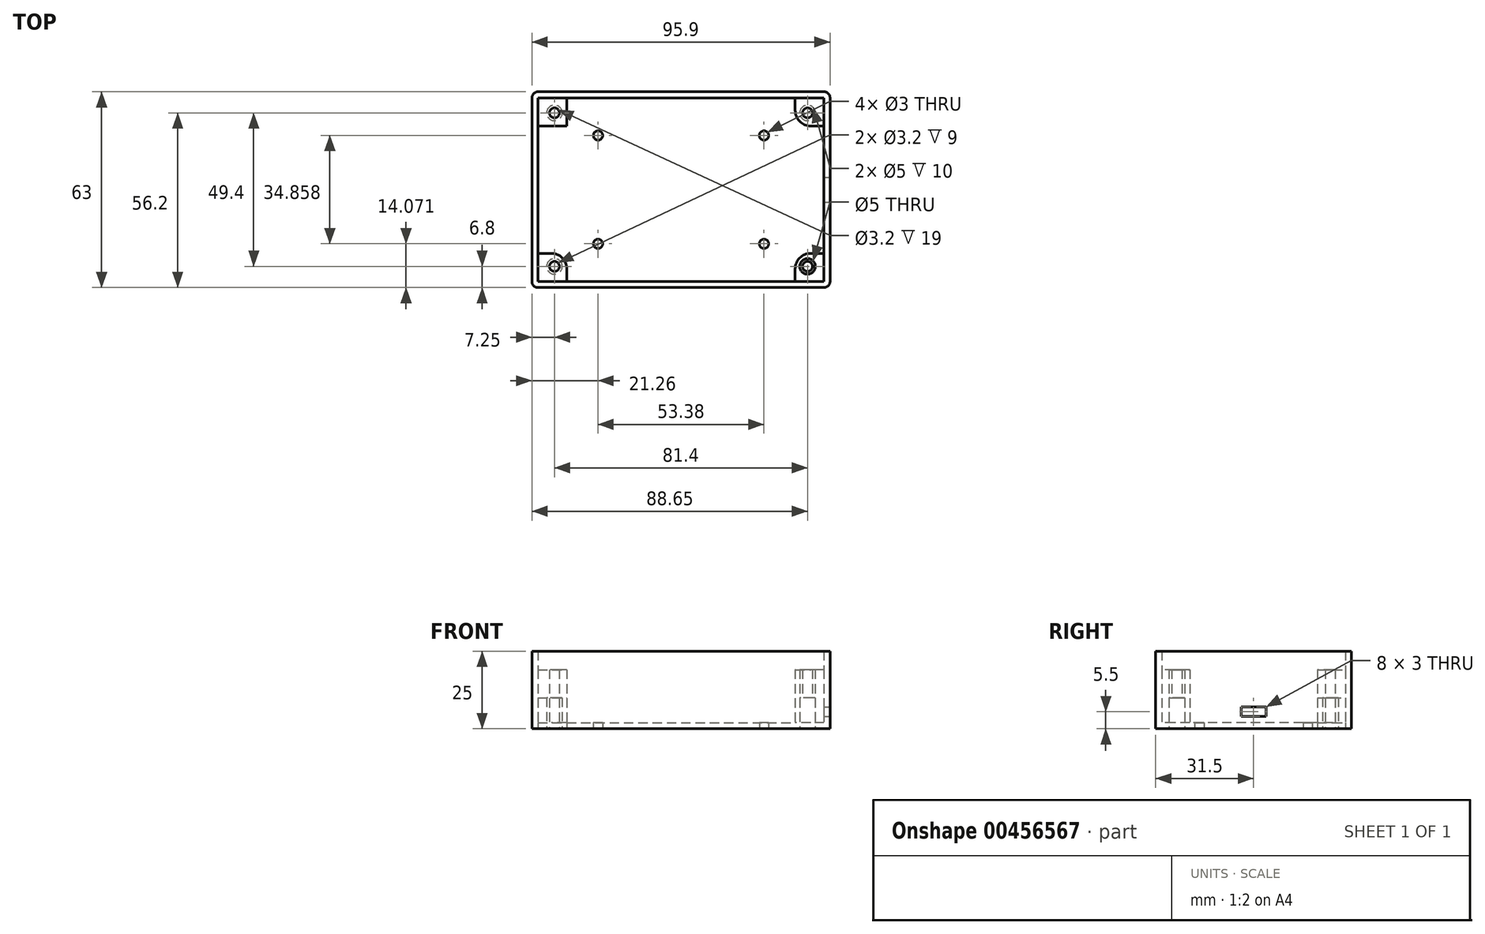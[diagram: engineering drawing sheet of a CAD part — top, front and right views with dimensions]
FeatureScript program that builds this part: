
annotation { "Feature Type Name" : "Feature", "Feature Type Description" : "" }
export const myFeature = defineFeature(function(context is Context, id is Id, definition is map)
    precondition{}
    {
        {
            var Q0;
            Q0=qCreatedBy(makeId("Top.planeOp"),FACE);
            var sketch = newSketch(context, id + "F0", { "sketchPlane" : qUnion([Q0])});
            skLineSegment(sketch, "E0", {"start": v(-47.95, 0) * mm, "end": v(-47.95, 31.5) * mm});
            skLineSegment(sketch, "E1", {"start": v(-47.95, 31.5) * mm, "end": v(0, 31.5) * mm});
            skLineSegment(sketch, "E2.MirrorCS", {"start": v(-47.95, -31.5) * mm, "end": v(0, -31.5) * mm});
            skLineSegment(sketch, "E3.MirrorCS", {"start": v(-47.95, 0) * mm, "end": v(-47.95, -31.5) * mm});
            skLineSegment(sketch, "E4.MirrorCS", {"start": v(47.95, 31.5) * mm, "end": v(0, 31.5) * mm});
            skLineSegment(sketch, "E5.MirrorCS", {"start": v(47.95, -31.5) * mm, "end": v(0, -31.5) * mm});
            skLineSegment(sketch, "E6.MirrorCS", {"start": v(47.95, 0) * mm, "end": v(47.95, -31.5) * mm});
            skLineSegment(sketch, "E7.MirrorCS", {"start": v(47.95, 0) * mm, "end": v(47.95, 31.5) * mm});
            skLineSegment(sketch, "E8", {"start": v(-46, 0) * mm, "end": v(-46, 29.5) * mm});
            skLineSegment(sketch, "E9", {"start": v(-46, 29.5) * mm, "end": v(0, 29.5) * mm});
            skLineSegment(sketch, "E10.MirrorCS", {"start": v(46, 29.5) * mm, "end": v(0, 29.5) * mm});
            skLineSegment(sketch, "E11.MirrorCS", {"start": v(46, 0) * mm, "end": v(46, 29.5) * mm});
            skLineSegment(sketch, "E12.MirrorCS", {"start": v(-46, 0) * mm, "end": v(-46, -29.5) * mm});
            skLineSegment(sketch, "E13.MirrorCS", {"start": v(-46, -29.5) * mm, "end": v(0, -29.5) * mm});
            skLineSegment(sketch, "E14.MirrorCS", {"start": v(46, -29.5) * mm, "end": v(0, -29.5) * mm});
            skLineSegment(sketch, "E15.MirrorCS", {"start": v(46, 0) * mm, "end": v(46, -29.5) * mm});
            skCircle(sketch, "E16", {"center": v(26.7, -17.43) * mm, "radius": 1.5 * mm});
            skCircle(sketch, "E17.MirrorC", {"center": v(-26.7, -17.43) * mm, "radius": 1.5 * mm});
            skCircle(sketch, "E18.MirrorC", {"center": v(-26.7, 17.43) * mm, "radius": 1.5 * mm});
            skCircle(sketch, "E19.MirrorC", {"center": v(26.7, 17.43) * mm, "radius": 1.5 * mm});
            skCircle(sketch, "E20", {"center": v(-40.7, -24.7) * mm, "radius": 1.6 * mm});
            skCircle(sketch, "E21", {"center": v(-40.7, -24.7) * mm, "radius": 2.5 * mm});
            skLineSegment(sketch, "E22", {"start": v(-46, -20.5) * mm, "end": v(-36.73, -20.5) * mm});
            skLineSegment(sketch, "E23", {"start": v(-36.73, -20.5) * mm, "end": v(-36.73, -29.5) * mm});
            skLineSegment(sketch, "E24.MirrorCS", {"start": v(36.73, -20.5) * mm, "end": v(36.73, -29.5) * mm});
            skLineSegment(sketch, "E25.MirrorCS", {"start": v(46, -20.5) * mm, "end": v(36.73, -20.5) * mm});
            skCircle(sketch, "E26.MirrorC", {"center": v(40.7, -24.7) * mm, "radius": 1.6 * mm});
            skCircle(sketch, "E27.MirrorC", {"center": v(40.7, -24.7) * mm, "radius": 2.5 * mm});
            skCircle(sketch, "E28.MirrorC", {"center": v(-40.7, 24.7) * mm, "radius": 2.5 * mm});
            skCircle(sketch, "E29.MirrorC", {"center": v(-40.7, 24.7) * mm, "radius": 1.6 * mm});
            skLineSegment(sketch, "E30.MirrorCS", {"start": v(-46, 20.5) * mm, "end": v(-36.73, 20.5) * mm});
            skLineSegment(sketch, "E31.MirrorCS", {"start": v(-36.73, 20.5) * mm, "end": v(-36.73, 29.5) * mm});
            skLineSegment(sketch, "E32.MirrorCS", {"start": v(46, 20.5) * mm, "end": v(36.73, 20.5) * mm});
            skLineSegment(sketch, "E33.MirrorCS", {"start": v(36.73, 20.5) * mm, "end": v(36.73, 29.5) * mm});
            skCircle(sketch, "E34.MirrorC", {"center": v(40.7, 24.7) * mm, "radius": 2.5 * mm});
            skCircle(sketch, "E35.MirrorC", {"center": v(40.7, 24.7) * mm, "radius": 1.6 * mm});
            skSolve(sketch);
        }
        {
            var Q0;
            Q0=makeQuery(id+"F0.imprint","IMPRINT",FACE,{"disambiguationData":[TD([[makeQuery(id+"F0.imprint","IMPRINT",EDGE,{"derivedFrom":sQuery(id+"F0.wireOp",EDGE,"E0")}),-1.0]])]});
            extrude(context, id + "F1", {"entities" : qUnion([Q0]), "depth" : 25 * mm});
        }
        {
            var Q0;
            Q0=makeQuery(id+"F1.opExtrude","SWEPT_EDGE",EDGE,{"disambiguationData":[OSD([sQuery(id+"F0.wireOp",EDGE,"E2.MirrorCS"),sQuery(id+"F0.wireOp",EDGE,"E3.MirrorCS")])]});
            fillet(context, id + "F2", {"entities" : qUnion([Q0]), "radius" : 2 * mm, "tangentPropagation" : true, "allowEdgeOverflow" : false});
        }
        {
            var Q0;
            Q0=makeQuery(id+"F1.opExtrude","SWEPT_EDGE",EDGE,{"disambiguationData":[OSD([sQuery(id+"F0.wireOp",EDGE,"E5.MirrorCS"),sQuery(id+"F0.wireOp",EDGE,"E6.MirrorCS")])]});
            var Q1;
            Q1=makeQuery(id+"F1.opExtrude","SWEPT_EDGE",EDGE,{"disambiguationData":[OSD([sQuery(id+"F0.wireOp",EDGE,"E4.MirrorCS"),sQuery(id+"F0.wireOp",EDGE,"E7.MirrorCS")])]});
            var Q2;
            Q2=makeQuery(id+"F1.opExtrude","SWEPT_EDGE",EDGE,{"disambiguationData":[OSD([sQuery(id+"F0.wireOp",EDGE,"E0"),sQuery(id+"F0.wireOp",EDGE,"E1")])]});
            fillet(context, id + "F3", {"entities" : qUnion([Q0, Q1, Q2]), "radius" : 2 * mm, "tangentPropagation" : true, "allowEdgeOverflow" : false});
        }
        {
            var Q0;
            Q0=makeQuery(id+"F0.imprint","IMPRINT",FACE,{"disambiguationData":[TD([[makeQuery(id+"F0.imprint","IMPRINT",EDGE,{"derivedFrom":sQuery(id+"F0.wireOp",EDGE,"E16")}),-1.0]])]});
            extrude(context, id + "F4", {"entities" : qUnion([Q0]), "operationType" : NewBodyOperationType.ADD, "depth" : 2 * mm});
        }
        {
            var Q0;
            Q0=makeQuery(id+"F0.imprint","IMPRINT",FACE,{"disambiguationData":[TD([[makeQuery(id+"F0.imprint","IMPRINT",EDGE,{"derivedFrom":sQuery(id+"F0.wireOp",EDGE,"E28.MirrorC")}),1.0]])]});
            var Q1;
            {var subQ1=sQuery(id+"F0.wireOp",EDGE,"E32.MirrorCS");Q1=makeQuery(id+"F0.imprint","IMPRINT",FACE,{"disambiguationData":[TD([[makeQuery(id+"F0.imprint","IMPRINT",EDGE,{"derivedFrom":subQ1}),-1.0]])]});}
            var Q2;
            {var subQ0=sQuery(id+"F0.wireOp",EDGE,"E24.MirrorCS");Q2=makeQuery(id+"F0.imprint","IMPRINT",FACE,{"disambiguationData":[TD([[makeQuery(id+"F0.imprint","IMPRINT",EDGE,{"derivedFrom":subQ0}),1.0]])]});}
            var Q3;
            Q3=makeQuery(id+"F0.imprint","IMPRINT",FACE,{"disambiguationData":[TD([[makeQuery(id+"F0.imprint","IMPRINT",EDGE,{"derivedFrom":sQuery(id+"F0.wireOp",EDGE,"E21")}),-1.0]])]});
            extrude(context, id + "F5", {"entities" : qUnion([Q0, Q1, Q2, Q3]), "operationType" : NewBodyOperationType.ADD, "depth" : 19 * mm});
        }
        {
            var Q0;
            Q0=makeQuery(id+"F5.opExtrude","SWEPT_EDGE",EDGE,{"disambiguationData":[OSD([sQuery(id+"F0.wireOp",EDGE,"E30.MirrorCS"),sQuery(id+"F0.wireOp",EDGE,"E31.MirrorCS")])]});
            var Q1;
            Q1=makeQuery(id+"F5.opExtrude","SWEPT_EDGE",EDGE,{"disambiguationData":[OSD([sQuery(id+"F0.wireOp",EDGE,"E32.MirrorCS"),sQuery(id+"F0.wireOp",EDGE,"E33.MirrorCS")])]});
            var Q2;
            Q2=makeQuery(id+"F5.opExtrude","SWEPT_EDGE",EDGE,{"disambiguationData":[OSD([sQuery(id+"F0.wireOp",EDGE,"E24.MirrorCS"),sQuery(id+"F0.wireOp",EDGE,"E25.MirrorCS")])]});
            var Q3;
            Q3=makeQuery(id+"F5.opExtrude","SWEPT_EDGE",EDGE,{"disambiguationData":[OSD([sQuery(id+"F0.wireOp",EDGE,"E22"),sQuery(id+"F0.wireOp",EDGE,"E23")])]});
            fillet(context, id + "F6", {"entities" : qUnion([Q0, Q1, Q2, Q3]), "radius" : 5 * mm, "tangentPropagation" : true, "allowEdgeOverflow" : false});
        }
        {
            var Q0;
            Q0=makeQuery(id+"F0.imprint","IMPRINT",FACE,{"disambiguationData":[TD([[makeQuery(id+"F0.imprint","IMPRINT",EDGE,{"derivedFrom":sQuery(id+"F0.wireOp",EDGE,"E28.MirrorC")}),-1.0]])]});
            var Q1;
            Q1=makeQuery(id+"F0.imprint","IMPRINT",FACE,{"disambiguationData":[TD([[makeQuery(id+"F0.imprint","IMPRINT",EDGE,{"derivedFrom":sQuery(id+"F0.wireOp",EDGE,"E34.MirrorC")}),1.0]])]});
            var Q2;
            Q2=makeQuery(id+"F0.imprint","IMPRINT",FACE,{"disambiguationData":[TD([[makeQuery(id+"F0.imprint","IMPRINT",EDGE,{"derivedFrom":sQuery(id+"F0.wireOp",EDGE,"E26.MirrorC")}),1.0]])]});
            var Q3;
            Q3=makeQuery(id+"F0.imprint","IMPRINT",FACE,{"disambiguationData":[TD([[makeQuery(id+"F0.imprint","IMPRINT",EDGE,{"derivedFrom":sQuery(id+"F0.wireOp",EDGE,"E20")}),-1.0]])]});
            extrude(context, id + "F7", {"entities" : qUnion([Q0, Q1, Q2, Q3]), "operationType" : NewBodyOperationType.ADD, "depth" : 19 * mm});
        }
        {
            var Q0;
            Q0=makeQuery(id+"F0.imprint","IMPRINT",FACE,{"disambiguationData":[TD([[makeQuery(id+"F0.imprint","IMPRINT",EDGE,{"derivedFrom":sQuery(id+"F0.wireOp",EDGE,"E28.MirrorC")}),-1.0]])]});
            var Q1;
            Q1=makeQuery(id+"F0.imprint","IMPRINT",FACE,{"disambiguationData":[TD([[makeQuery(id+"F0.imprint","IMPRINT",EDGE,{"derivedFrom":sQuery(id+"F0.wireOp",EDGE,"E20")}),-1.0]])]});
            var Q2;
            Q2=makeQuery(id+"F0.imprint","IMPRINT",FACE,{"disambiguationData":[TD([[makeQuery(id+"F0.imprint","IMPRINT",EDGE,{"derivedFrom":sQuery(id+"F0.wireOp",EDGE,"E26.MirrorC")}),1.0]])]});
            var Q3;
            Q3=makeQuery(id+"F0.imprint","IMPRINT",FACE,{"disambiguationData":[TD([[makeQuery(id+"F0.imprint","IMPRINT",EDGE,{"derivedFrom":sQuery(id+"F0.wireOp",EDGE,"E34.MirrorC")}),1.0]])]});
            extrude(context, id + "F8", {"entities" : qUnion([Q0, Q1, Q2, Q3]), "operationType" : NewBodyOperationType.REMOVE, "depth" : 10 * mm});
        }
        {
            var Q0;
            Q0=makeQuery(id+"F1.opExtrude","SWEPT_FACE",FACE,{"disambiguationData":[OSD([sQuery(id+"F0.wireOp",EDGE,"E6.MirrorCS"),sQuery(id+"F0.wireOp",EDGE,"E7.MirrorCS")])]});
            var sketch = newSketch(context, id + "F9", { "sketchPlane" : qUnion([Q0])});
            skLineSegment(sketch, "E36", {"start": v(0, 4) * mm, "end": v(-4, 4) * mm});
            skLineSegment(sketch, "E37", {"start": v(-4, 4) * mm, "end": v(-4, 7) * mm});
            skLineSegment(sketch, "E38", {"start": v(-4, 7) * mm, "end": v(0, 7) * mm});
            skLineSegment(sketch, "E39", {"start": v(0, 4) * mm, "end": v(0, 0) * mm});
            skLineSegment(sketch, "E40.MirrorCS", {"start": v(4, 7) * mm, "end": v(0, 7) * mm});
            skLineSegment(sketch, "E41.MirrorCS", {"start": v(4, 4) * mm, "end": v(4, 7) * mm});
            skLineSegment(sketch, "E42.MirrorCS", {"start": v(0, 4) * mm, "end": v(4, 4) * mm});
            skSolve(sketch);
        }
        {
            var Q0;
            Q0=makeQuery(id+"F9.imprint","IMPRINT",FACE,{"disambiguationData":[TD([[makeQuery(id+"F9.imprint","IMPRINT",EDGE,{"derivedFrom":sQuery(id+"F9.wireOp",EDGE,"E36")}),-1.0]])]});
            extrude(context, id + "F10", {"entities" : qUnion([Q0]), "operationType" : NewBodyOperationType.REMOVE, "oppositeDirection" : true, "depth" : 25 * mm});
        }
    });
